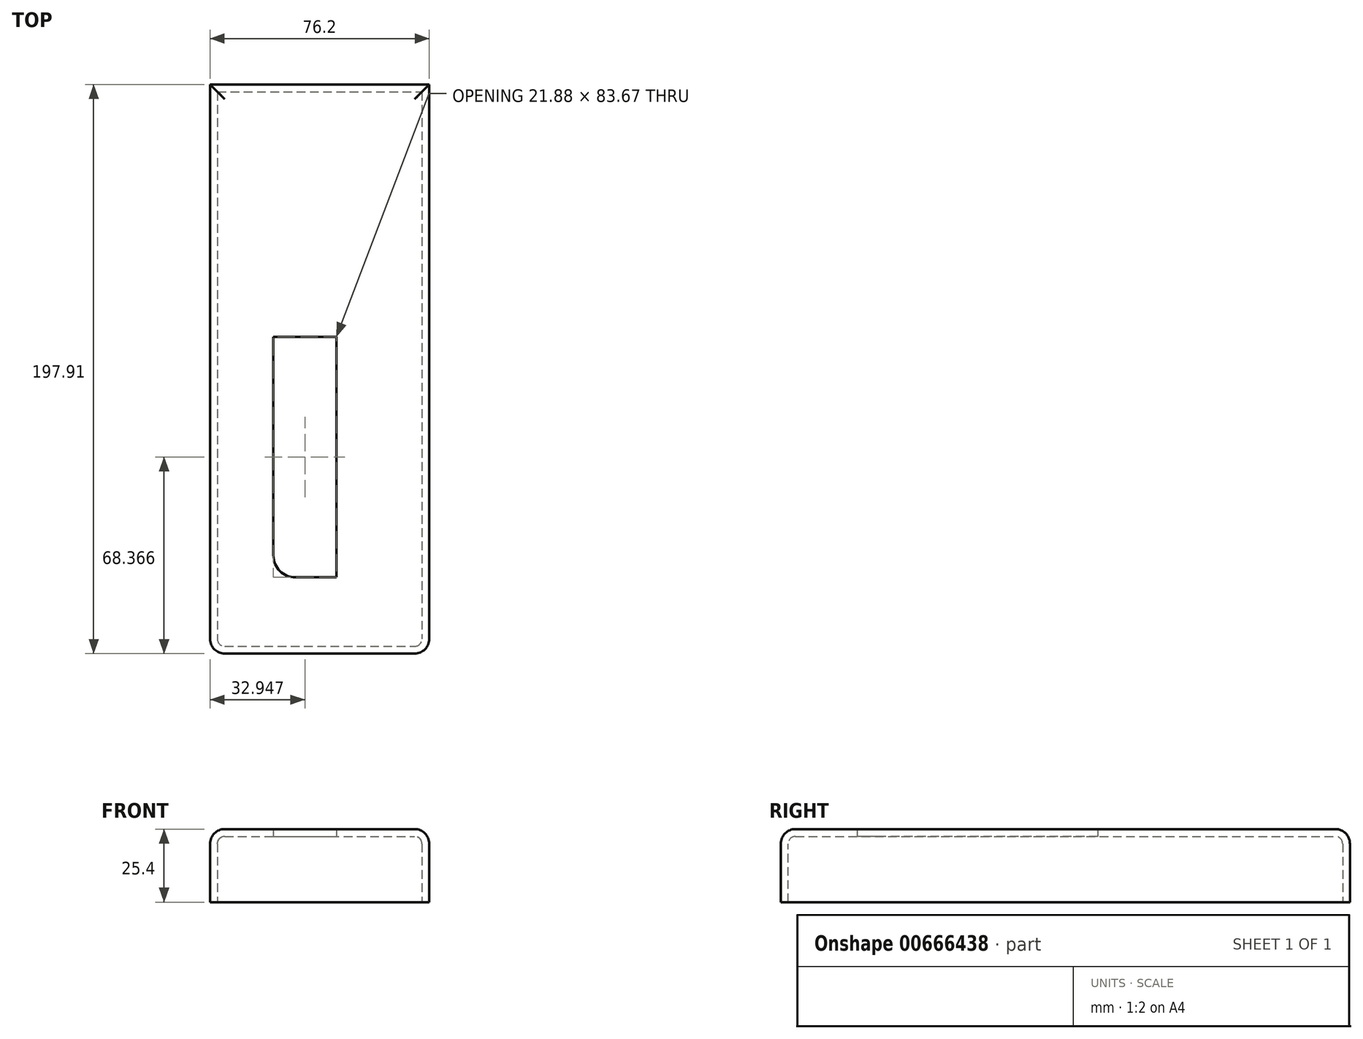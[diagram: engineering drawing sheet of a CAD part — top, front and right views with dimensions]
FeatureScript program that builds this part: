
annotation { "Feature Type Name" : "Feature", "Feature Type Description" : "" }
export const myFeature = defineFeature(function(context is Context, id is Id, definition is map)
    precondition{}
    {
        {
            var Q0;
            Q0=qCreatedBy(makeId("Top.planeOp"),FACE);
            var sketch = newSketch(context, id + "F0", { "sketchPlane" : qUnion([Q0])});
            skLineSegment(sketch, "E0.bottom", {"start": v(-35.2, 36.64) * mm, "end": v(41, 36.64) * mm});
            skLineSegment(sketch, "E0.top", {"start": v(-35.2, -34.27) * mm, "end": v(41, -34.27) * mm});
            skLineSegment(sketch, "E0.left", {"start": v(-35.2, 36.64) * mm, "end": v(-35.2, -34.27) * mm});
            skLineSegment(sketch, "E0.right", {"start": v(41, 36.64) * mm, "end": v(41, -34.27) * mm});
            skSolve(sketch);
        }
        {
            var Q0;
            Q0=makeQuery(id+"F0.imprint","IMPRINT",FACE,{"disambiguationData":[TD([[makeQuery(id+"F0.imprint","IMPRINT",EDGE,{"derivedFrom":sQuery(id+"F0.wireOp",EDGE,"E0.bottom")}),-1.0]])]});
            extrude(context, id + "F1", {"entities" : qUnion([Q0]), "depth" : 25.4 * mm, "offsetDistance" : 25.4 * mm});
        }
        {
            var Q0;
            Q0=makeQuery(id+"F1.opExtrude","SWEPT_FACE",FACE,{"disambiguationData":[OSD([sQuery(id+"F0.wireOp",EDGE,"E0.top")])]});
            extrude(context, id + "F2", {"entities" : qUnion([Q0]), "operationType" : NewBodyOperationType.ADD, "depth" : 127 * mm, "offsetDistance" : 25.4 * mm});
        }
        {
            var Q0;
            {var subQ0=sQuery(id+"F0.wireOp",EDGE,"E0.top");Q0=makeQuery(id+"F2.boolean.opBoolean","MERGE",FACE,{"derivedFrom":[makeQuery(id+"F1.opExtrude","CAP_FACE",FACE,{"disambiguationData":[OSD([sQuery(id+"F0.wireOp",EDGE,"E0.bottom"),subQ0,sQuery(id+"F0.wireOp",EDGE,"E0.left"),sQuery(id+"F0.wireOp",EDGE,"E0.right")])],"isStart":false}),makeQuery(id+"F2.opExtrude","SWEPT_FACE",FACE,{"disambiguationData":[OSD([subQ0]),TDD([makeQuery(id+"F1.opExtrude","CAP_EDGE",EDGE,{"disambiguationData":[OSD([subQ0])],"isStart":false})])]})]});}
            var Q1;
            Q1=makeQuery(id+"F2.opExtrude","CAP_EDGE",EDGE,{"disambiguationData":[OSD([sQuery(id+"F0.wireOp",EDGE,"E0.top"),sQuery(id+"F0.wireOp",EDGE,"E0.right")])],"isStart":false});
            var Q2;
            Q2=makeQuery(id+"F2.opExtrude","CAP_EDGE",EDGE,{"disambiguationData":[OSD([sQuery(id+"F0.wireOp",EDGE,"E0.top"),sQuery(id+"F0.wireOp",EDGE,"E0.left")])],"isStart":false});
            fillet(context, id + "F3", {"entities" : qUnion([Q0, Q1, Q2]), "radius" : 5.08 * mm, "tangentPropagation" : true, "allowEdgeOverflow" : false});
        }
        {
            var Q0;
            {var subQ0=sQuery(id+"F0.wireOp",EDGE,"E0.top");Q0=makeQuery(id+"F2.boolean.opBoolean","MERGE",FACE,{"derivedFrom":[makeQuery(id+"F1.opExtrude","CAP_FACE",FACE,{"disambiguationData":[OSD([sQuery(id+"F0.wireOp",EDGE,"E0.bottom"),subQ0,sQuery(id+"F0.wireOp",EDGE,"E0.left"),sQuery(id+"F0.wireOp",EDGE,"E0.right")])],"isStart":true}),makeQuery(id+"F2.opExtrude","SWEPT_FACE",FACE,{"disambiguationData":[OSD([subQ0]),TDD([makeQuery(id+"F1.opExtrude","CAP_EDGE",EDGE,{"disambiguationData":[OSD([subQ0])],"isStart":true})])]})]});}
            var sketch = newSketch(context, id + "F4", { "sketchPlane" : qUnion([Q0])});
            skLineSegment(sketch, "E1.bottom", {"start": v(8.7, 134.74) * mm, "end": v(-13.18, 134.74) * mm});
            skLineSegment(sketch, "E1.top", {"start": v(8.7, 51.07) * mm, "end": v(-13.18, 51.07) * mm});
            skLineSegment(sketch, "E1.left", {"start": v(8.7, 134.74) * mm, "end": v(8.7, 51.07) * mm});
            skLineSegment(sketch, "E1.right", {"start": v(-13.18, 134.74) * mm, "end": v(-13.18, 51.07) * mm});
            skSolve(sketch);
        }
        {
            var Q0;
            {var subQ0=sQuery(id+"F0.wireOp",EDGE,"E0.top");Q0=makeQuery(id+"F2.boolean.opBoolean","MERGE",FACE,{"derivedFrom":[makeQuery(id+"F1.opExtrude","CAP_FACE",FACE,{"disambiguationData":[OSD([sQuery(id+"F0.wireOp",EDGE,"E0.bottom"),subQ0,sQuery(id+"F0.wireOp",EDGE,"E0.left"),sQuery(id+"F0.wireOp",EDGE,"E0.right")])],"isStart":true}),makeQuery(id+"F2.opExtrude","SWEPT_FACE",FACE,{"disambiguationData":[OSD([subQ0]),TDD([makeQuery(id+"F1.opExtrude","CAP_EDGE",EDGE,{"disambiguationData":[OSD([subQ0])],"isStart":true})])]})]});}
            shell(context, id + "F5", {"entities" : qUnion([Q0]), "thickness" : 2.54 * mm});
        }
        {
            var Q0;
            Q0=makeQuery(id+"F4.imprint","IMPRINT",FACE,{"disambiguationData":[TD([[makeQuery(id+"F4.imprint","IMPRINT",EDGE,{"derivedFrom":sQuery(id+"F4.wireOp",EDGE,"E1.bottom")}),1.0]])]});
            extrude(context, id + "F6", {"entities" : qUnion([Q0]), "operationType" : NewBodyOperationType.REMOVE, "oppositeDirection" : true, "depth" : 25.4 * mm, "offsetDistance" : 25.4 * mm});
        }
        {
            var Q0;
            Q0=makeQuery(id+"F6.boolean.opBoolean","COPY",EDGE,{"derivedFrom":makeQuery(id+"F6.opExtrude","SWEPT_EDGE",EDGE,{"disambiguationData":[OSD([sQuery(id+"F4.wireOp",EDGE,"E1.bottom"),sQuery(id+"F4.wireOp",EDGE,"E1.right")])]})});
            fillet(context, id + "F7", {"entities" : qUnion([Q0]), "radius" : 7.62 * mm, "tangentPropagation" : true, "allowEdgeOverflow" : false});
        }
    });
